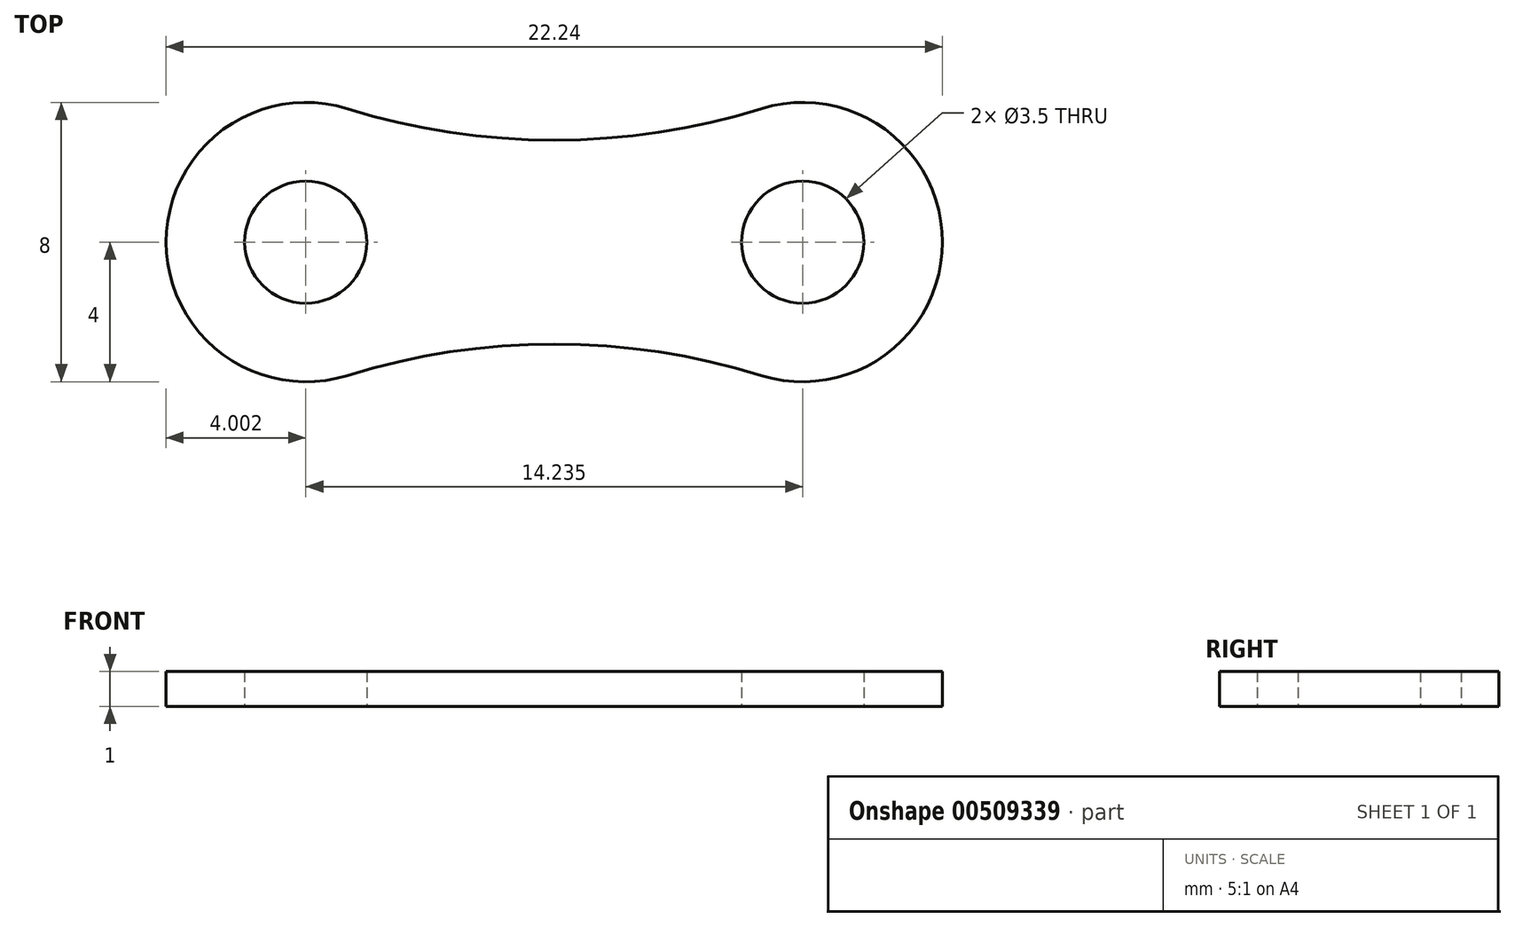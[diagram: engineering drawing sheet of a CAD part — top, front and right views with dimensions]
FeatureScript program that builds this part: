
annotation { "Feature Type Name" : "Feature", "Feature Type Description" : "" }
export const myFeature = defineFeature(function(context is Context, id is Id, definition is map)
    precondition{}
    {
        {
            var Q0;
            Q0=qCreatedBy(makeId("Top.planeOp"),FACE);
            var sketch = newSketch(context, id + "F0", { "sketchPlane" : qUnion([Q0])});
            skArc(sketch, "E0", {"start": v(-5.93, 3.82) * mm, "mid": v(-11.12, 0) * mm, "end": v(-5.93, -3.82) * mm});
            skArc(sketch, "E1", {"start": v(5.93, -3.82) * mm, "mid": v(11.12, 0) * mm, "end": v(5.93, 3.82) * mm});
            skArc(sketch, "E2", {"start": v(-5.93, 3.82) * mm, "mid": v(0, 2.92) * mm, "end": v(5.93, 3.82) * mm});
            skArc(sketch, "E3", {"start": v(5.93, -3.82) * mm, "mid": v(0, -2.92) * mm, "end": v(-5.93, -3.82) * mm});
            skCircle(sketch, "E4", {"center": v(-7.12, 0) * mm, "radius": 1.75 * mm});
            skCircle(sketch, "E5", {"center": v(7.12, 0) * mm, "radius": 1.75 * mm});
            skLineSegment(sketch, "E6", {"start": v(-7.12, 0) * mm, "end": v(0, 0) * mm, "construction": true});
            skLineSegment(sketch, "E7", {"start": v(0, 0) * mm, "end": v(7.12, 0) * mm, "construction": true});
            skSolve(sketch);
        }
        {
            var Q0;
            Q0=makeQuery(id+"F0.imprint","IMPRINT",FACE,{"disambiguationData":[TD([[makeQuery(id+"F0.imprint","IMPRINT",EDGE,{"derivedFrom":sQuery(id+"F0.wireOp",EDGE,"E0")}),1.0]])]});
            extrude(context, id + "F1", {"entities" : qUnion([Q0]), "depth" : 1 * mm});
        }
    });
